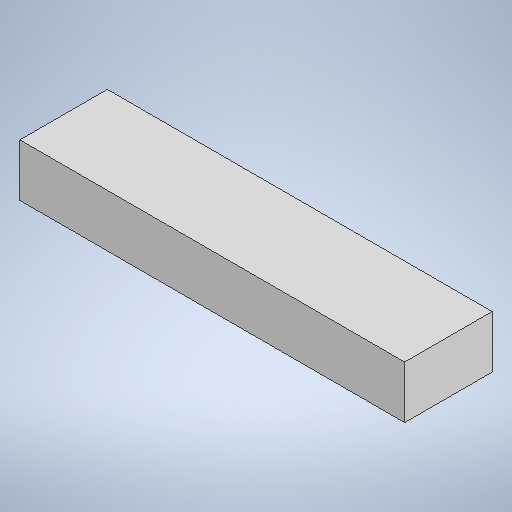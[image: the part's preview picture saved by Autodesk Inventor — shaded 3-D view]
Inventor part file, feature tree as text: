
AUTODESK INVENTOR PART (.ipt)
format: ipt  version: 2025.1 (Build 291241020, 241B)  size: 210,432 bytes
history: native  units: in
note: dims shown in document units (in); Inventor stores cm internally (conversion verified against a paired STEP export)
features: extrude x1, sketch x1
ambient origin geometry x8: Origin, YZ Plane, XZ Plane, XY Plane, X Axis, Y Axis, Z Axis, Center Point
bodies: Solid1 (feature_tree)
feature tree (2):
  extrude  "Extrusion1"  Depth=1.2992in
  sketch  "Sketch1"  dims[d0=0.2953in d1=1.2992in d2=0.1772in d3=0.0in d4=0.0197in d5=0.0344in]
